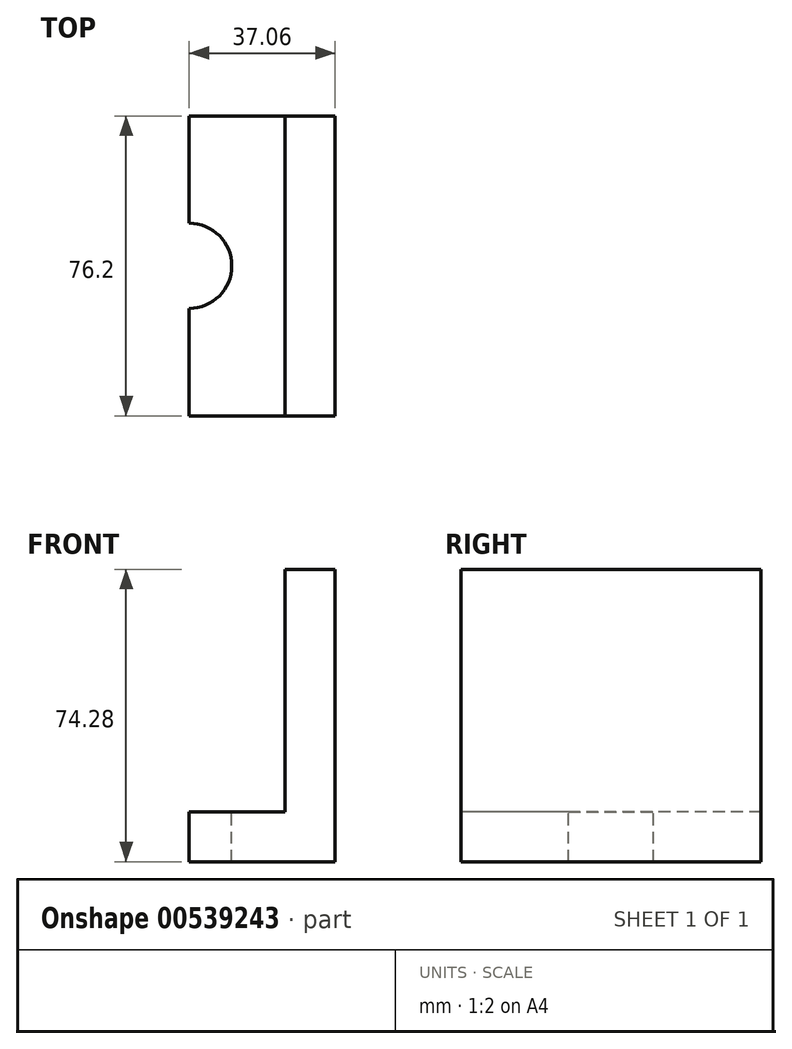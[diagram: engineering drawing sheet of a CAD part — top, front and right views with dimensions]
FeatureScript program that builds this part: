
annotation { "Feature Type Name" : "Feature", "Feature Type Description" : "" }
export const myFeature = defineFeature(function(context is Context, id is Id, definition is map)
    precondition{}
    {
        {
            var Q0;
            Q0=qCreatedBy(makeId("Front.planeOp"),FACE);
            var sketch = newSketch(context, id + "F0", { "sketchPlane" : qUnion([Q0])});
            skLineSegment(sketch, "E0", {"start": v(0, -42.95) * mm, "end": v(37.06, -42.95) * mm});
            skLineSegment(sketch, "E1", {"start": v(37.06, -42.95) * mm, "end": v(37.06, 31.33) * mm});
            skLineSegment(sketch, "E2", {"start": v(0, -30.25) * mm, "end": v(24.36, -30.25) * mm});
            skLineSegment(sketch, "E3", {"start": v(24.36, 31.33) * mm, "end": v(24.36, -30.25) * mm});
            skLineSegment(sketch, "E4", {"start": v(37.06, 31.33) * mm, "end": v(24.36, 31.33) * mm});
            skLineSegment(sketch, "E5", {"start": v(0, -30.25) * mm, "end": v(0, -42.95) * mm});
            skSolve(sketch);
        }
        {
            var Q0;
            Q0=makeQuery(id+"F0.imprint","IMPRINT",FACE,{"disambiguationData":[TD([[makeQuery(id+"F0.imprint","IMPRINT",EDGE,{"derivedFrom":sQuery(id+"F0.wireOp",EDGE,"E0")}),1.0]])]});
            extrude(context, id + "F1", {"entities" : qUnion([Q0]), "oppositeDirection" : true, "depth" : 76.2 * mm, "offsetDistance" : 25.4 * mm});
        }
        {
            var Q0;
            Q0=makeQuery(id+"F1.opExtrude","SWEPT_FACE",FACE,{"disambiguationData":[OSD([sQuery(id+"F0.wireOp",EDGE,"E2")])]});
            var sketch = newSketch(context, id + "F2", { "sketchPlane" : qUnion([Q0])});
            skCircle(sketch, "E6", {"center": v(0, 38.1) * mm, "radius": 10.8 * mm});
            skSolve(sketch);
        }
        {
            var Q0;
            {var subQ0=sQuery(id+"F2.wireOp",EDGE,"E6");var subQ1=makeQuery(id+"F1.opExtrude","SWEPT_EDGE",EDGE,{"disambiguationData":[OSD([sQuery(id+"F0.wireOp",EDGE,"E2"),sQuery(id+"F0.wireOp",EDGE,"E5")])]});var subQ2=makeQuery(id+"F2.imprint","INTERSECT",VERTEX,{"disambiguationData":[OD(0.0)],"derivedFrom":[subQ1,subQ0]});Q0=makeQuery(id+"F2.imprint","IMPRINT",FACE,{"disambiguationData":[TD([[makeQuery(id+"F2.imprint","IMPRINT",EDGE,{"disambiguationData":[TD([[subQ2,-1.0]])],"derivedFrom":subQ0}),1.0]])]});}
            extrude(context, id + "F3", {"entities" : qUnion([Q0]), "operationType" : NewBodyOperationType.REMOVE, "oppositeDirection" : true, "depth" : 39.62 * mm, "offsetDistance" : 25.4 * mm});
        }
    });
